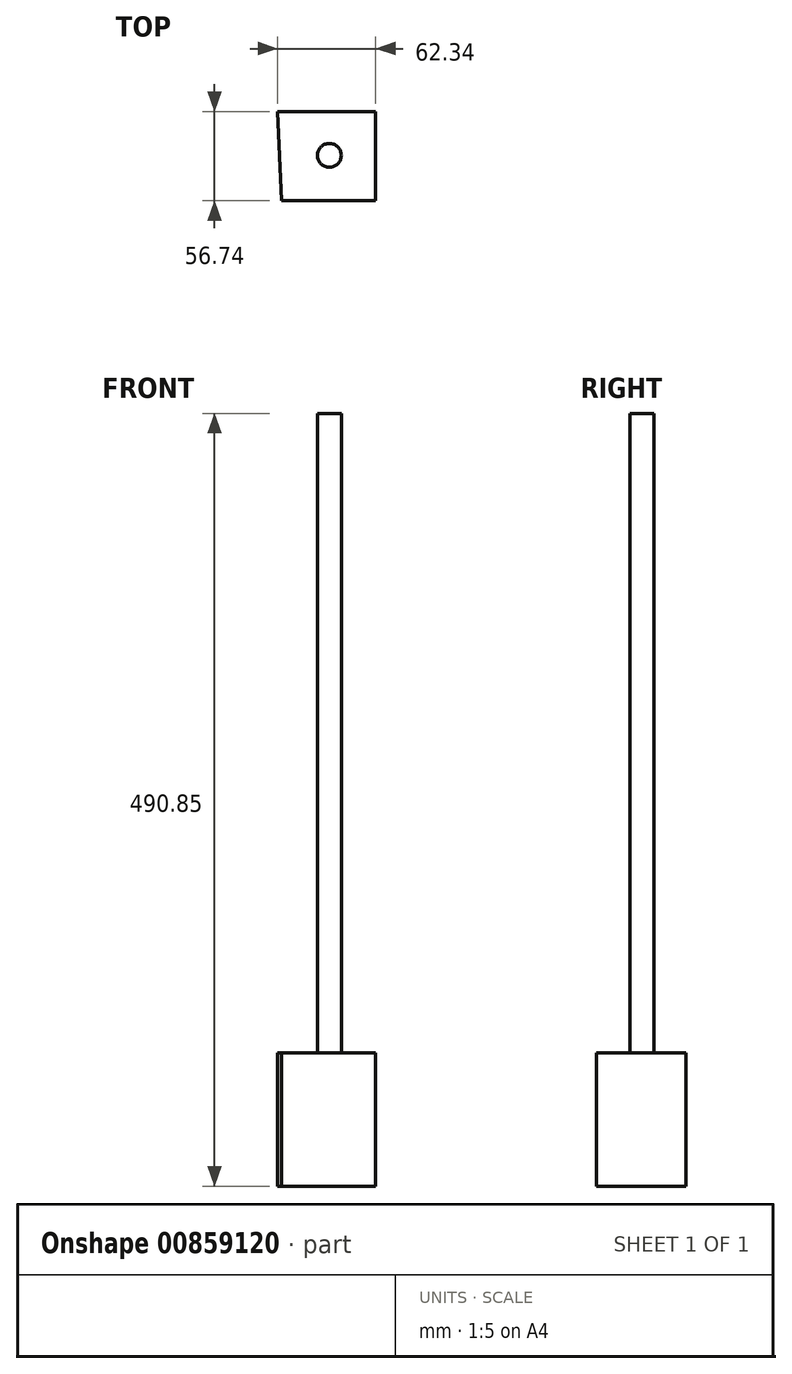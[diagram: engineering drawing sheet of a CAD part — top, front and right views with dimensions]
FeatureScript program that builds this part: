
annotation { "Feature Type Name" : "Feature", "Feature Type Description" : "" }
export const myFeature = defineFeature(function(context is Context, id is Id, definition is map)
    precondition{}
    {
        {
            var Q0;
            Q0=qCreatedBy(makeId("Top.planeOp"),FACE);
            var sketch = newSketch(context, id + "F0", { "sketchPlane" : qUnion([Q0])});
            skLineSegment(sketch, "E0", {"start": v(-32.9, 27.87) * mm, "end": v(29.43, 27.87) * mm});
            skLineSegment(sketch, "E1", {"start": v(29.43, 27.87) * mm, "end": v(29.43, -28.87) * mm});
            skLineSegment(sketch, "E2", {"start": v(29.43, -28.87) * mm, "end": v(-30.33, -28.87) * mm});
            skLineSegment(sketch, "E3", {"start": v(-30.33, -28.87) * mm, "end": v(-32.9, 27.87) * mm});
            skSolve(sketch);
        }
        {
            var Q0;
            Q0=makeQuery(id+"F0.imprint","IMPRINT",FACE,{"disambiguationData":[TD([[makeQuery(id+"F0.imprint","IMPRINT",EDGE,{"derivedFrom":sQuery(id+"F0.wireOp",EDGE,"E0")}),-1.0]])]});
            extrude(context, id + "F1", {"entities" : qUnion([Q0]), "oppositeDirection" : true, "depth" : 84.76 * mm, "offsetDistance" : 25.4 * mm});
        }
        {
            var Q0;
            Q0=qCreatedBy(makeId("Top.planeOp"),FACE);
            var sketch = newSketch(context, id + "F2", { "sketchPlane" : qUnion([Q0])});
            skCircle(sketch, "E4", {"center": v(0, 0) * mm, "radius": 7.59 * mm});
            skSolve(sketch);
        }
        {
            var Q0;
            Q0 = qSketchRegion(id + "F2", true);
            extrude(context, id + "F3", {"entities" : qUnion([Q0]), "operationType" : NewBodyOperationType.ADD, "depth" : 406.1 * mm, "offsetDistance" : 25.4 * mm});
        }
        {
            var Q0;
            Q0=qCreatedBy(makeId("Front.planeOp"),FACE);
            var sketch = newSketch(context, id + "F4", { "sketchPlane" : qUnion([Q0])});
            skLineSegment(sketch, "E5", {"start": v(0, -42.88) * mm, "end": v(122.54, -42.88) * mm});
            skLineSegment(sketch, "E6", {"start": v(122.54, -42.88) * mm, "end": v(83.2, -22.92) * mm});
            skLineSegment(sketch, "E7", {"start": v(83.2, -22.92) * mm, "end": v(0, -22.92) * mm});
            skLineSegment(sketch, "E8", {"start": v(0, -22.92) * mm, "end": v(0, -42.88) * mm});
            skSolve(sketch);
        }
        {
            var Q0;
            Q0=sQuery(id+"F4.wireOp",EDGE,"E7");
            var Q1;
            Q1=sQuery(id+"F4.wireOp",EDGE,"E6");
            var Q2;
            Q2=sQuery(id+"F4.wireOp",EDGE,"E8");
            var Q3;
            Q3=sQuery(id+"F4.wireOp",EDGE,"E5");
            extrude(context, id + "F5", {"bodyType" : ToolBodyType.SURFACE, "surfaceEntities" : qUnion([Q0, Q1, Q2, Q3]), "oppositeDirection" : true, "depth" : 6.54 * mm, "offsetDistance" : 25.4 * mm});
        }
    });
